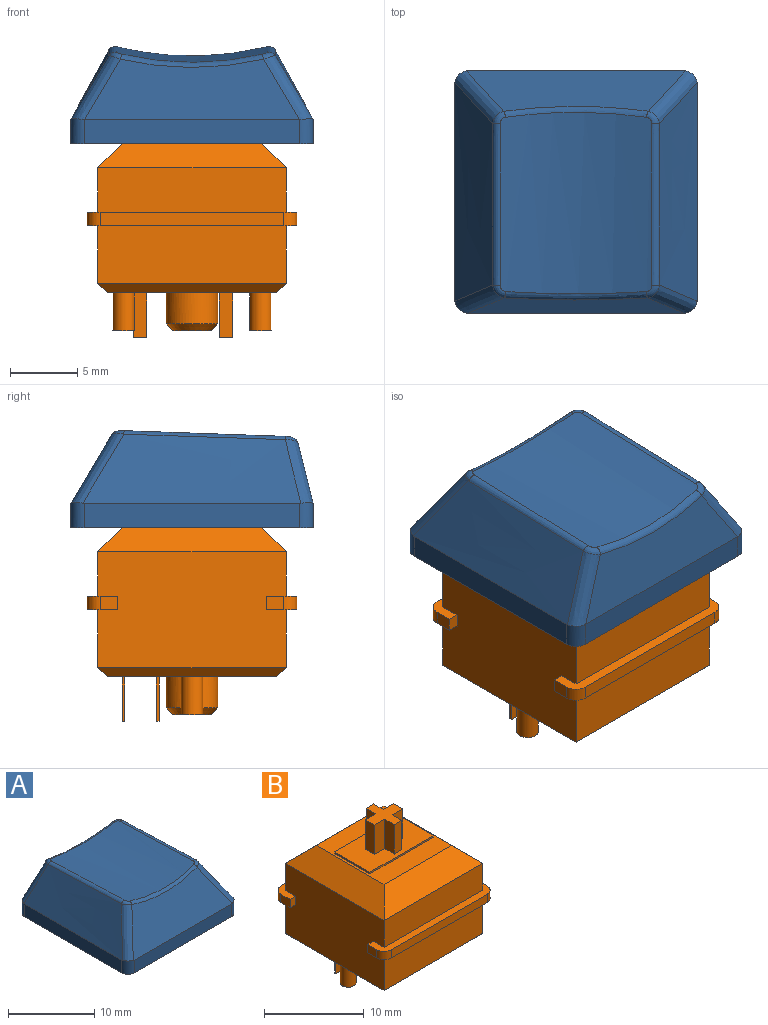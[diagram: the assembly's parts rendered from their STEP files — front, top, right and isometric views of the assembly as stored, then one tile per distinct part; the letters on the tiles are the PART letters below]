
ASSEMBLY  parts=2 mates=1
PART A: 50 faces, bbox 21.6x21x10.3 mm
  f0: plane 18x18mm, normal (0,0,-1), area 67.1mm2, adj f1,f2,f3,f4,f10,f12,f14,f16
  f1: plane 16x1.8mm, normal (1,0,0), area 28.8mm2, adj f0,f8,f10,f16
  f2: plane 16x1.8mm, normal (0,1,0), area 28.8mm2, adj f0,f5,f14,f15,f16,f17
  f3: plane 16x1.8mm, normal (-1,0,0), area 28.8mm2, adj f0,f6,f12,f14
  f4: plane 16x1.8mm, normal (0,-1,0), area 28.8mm2, adj f0,f7,f10,f12
  f5: plane 15.96x4.48mm, normal (0,0.97,0.24), area 56.8mm2, adj f2,f15,f17,f20
  f6: bspline ~18x5.51mm, area 80.2mm2, adj f3,f12,f13,f14,f15,f19
  f7: plane 16.27x5.09mm, normal (0,-0.86,0.51), area 74.6mm2, adj f4,f10,f11,f12,f13,f23
  f8: bspline ~18x5.51mm, area 80.2mm2, adj f1,f10,f11,f16,f17,f24
  f9: cylinder r=22.9mm len=13.32mm, axis (0,1,-0.04), area 149.5mm2, adj f18,f19,f20,f21,f22,f23,f24,f25
  f10: cylinder r=1mm len=1.89mm, axis (0,0,-1), area 2.9mm2, adj f0,f1,f4,f7,f8,f11
  f11: bspline ~6.77x4.7mm, area 8.7mm2, adj f7,f8,f10,f25
  f12: cylinder r=1mm len=1.89mm, axis (0,0,1), area 2.9mm2, adj f0,f3,f4,f6,f7,f13
  f13: bspline ~6.77x4.7mm, area 8.7mm2, adj f6,f7,f12,f21
  f14: cylinder r=1mm len=1.81mm, axis (0,0,-1), area 2.8mm2, adj f0,f2,f3,f6,f15
  f15: bspline ~8.13x5.44mm, area 7.9mm2, adj f2,f5,f6,f14,f18
  f16: cylinder r=1mm len=1.81mm, axis (0,0,1), area 2.8mm2, adj f0,f1,f2,f8,f17
  f17: bspline ~8.13x5.44mm, area 7.9mm2, adj f2,f5,f8,f16,f22
  f18: bspline ~1.19x1.01mm, area 0.7mm2, adj f9,f15,f19,f20
  f19: bspline ~16.72x0.91mm, area 7.8mm2, adj f6,f9,f18,f21
  f20: bspline ~10.66x0.99mm, area 6.9mm2, adj f5,f9,f18,f22
  f21: bspline ~1.2x1.09mm, area 0.6mm2, adj f9,f13,f19,f23
  f22: bspline ~1.17x1.02mm, area 0.7mm2, adj f9,f17,f20,f24
  f23: bspline ~10.72x0.84mm, area 5.8mm2, adj f7,f9,f21,f25
  f24: bspline ~16.72x0.91mm, area 7.8mm2, adj f8,f9,f22,f25
  f25: bspline ~1.2x1.09mm, area 0.6mm2, adj f9,f11,f23,f24
  f26: plane 16.02x1.56mm, normal (-1,0,0), area 24.6mm2, adj f0,f27,f29,f33
  f27: plane 16x1.68mm, normal (0,-1,0), area 26.8mm2, adj f0,f26,f28,f30,f31,f33
  f28: plane 16.02x1.56mm, normal (1,0,0), area 24.6mm2, adj f0,f27,f29,f31
  f29: plane 16.02x1.54mm, normal (0,1,0), area 24.4mm2, adj f0,f26,f28,f32
  f30: plane 16.19x4.4mm, normal (0,-0.97,-0.24), area 50.7mm2, adj f27,f31,f33,f34
  f31: offset ~20x7.51mm, area 71.4mm2, adj f27,f28,f30,f32,f34
  f32: plane 16.71x5.3mm, normal (0,0.86,-0.51), area 66.9mm2, adj f29,f31,f33,f34
  f33: offset ~20x7.51mm, area 71.4mm2, adj f26,f27,f30,f32,f34
  f34: cylinder r=23.9mm len=12.29mm, axis (0,1,-0.04), area 112.6mm2, adj f30,f31,f32,f33,f46
  f35: plane 4.69x1.5mm, normal (-1,0,0), area 7mm2, adj f36,f44,f45,f49
  f36: plane 4.78x1.5mm, normal (0,-1,0), area 7.1mm2, adj f35,f37,f45,f49
  f37: plane 4.82x1.3mm, normal (-1,0,0), area 6.2mm2, adj f36,f38,f45,f49
  f38: plane 4.82x1.5mm, normal (0,1,0), area 7.2mm2, adj f37,f39,f45,f49
  f39: plane 4.79x1.5mm, normal (-1,0,0), area 7.1mm2, adj f38,f40,f45,f49
  f40: plane 4.79x1.3mm, normal (0,1,0), area 6.2mm2, adj f39,f41,f45,f49
  f41: plane 4.79x1.5mm, normal (1,0,0), area 7.1mm2, adj f40,f42,f45,f49
  f42: plane 4.82x1.5mm, normal (0,1,0), area 7.2mm2, adj f41,f43,f45,f49
  f43: plane 4.82x1.3mm, normal (1,0,0), area 6.2mm2, adj f42,f45,f47,f49
  f44: plane 4.64x1.3mm, normal (0,-1,0), area 6mm2, adj f35,f45,f48,f49
  f45: plane 5.5x5.5mm, normal (0,0,-1), area 14.3mm2, adj f35,f36,f37,f38,f39,f40,f41,f42
  f46: cylinder r=2.75mm len=5.5mm, axis (0,0,-1), area 84mm2, adj f34,f45
  f47: plane 4.78x1.5mm, normal (0,-1,0), area 7.1mm2, adj f43,f45,f48,f49
  f48: plane 4.69x1.5mm, normal (1,0,0), area 7mm2, adj f44,f45,f47,f49
  f49: cylinder r=23.9mm len=4.3mm, axis (0,1,-0.04), area 9.5mm2, adj f35,f36,f37,f38,f39,f40,f41,f42
PART B: 69 faces, bbox 15.6x15.6x18.6 mm
  f0: plane 15.6x2.3mm, normal (0,0,-1), area 14.4mm2, adj f2,f3,f28,f30,f35,f60,f62,f63
  f1: plane 15.6x2.3mm, normal (0,0,-1), area 14.4mm2, adj f28,f30,f33,f34,f36,f59,f61,f64
  f2: plane 1.3x1mm, normal (1,0,0), area 1.3mm2, adj f0,f32,f62,f66
  f3: plane 1.3x1mm, normal (-1,0,0), area 1.3mm2, adj f0,f32,f63,f68
  f4: plane 15.6x2.3mm, normal (0,0,1), area 14.4mm2, adj f28,f30,f31,f33,f34,f36,f61,f64
  f5: plane 14x2.2mm, normal (-0.71,0,0.71), area 36.7mm2, adj f6,f7,f26,f30
  f6: plane 14x2.2mm, normal (0,-0.71,0.71), area 36.7mm2, adj f5,f7,f27,f31
  f7: plane 9.6x9.6mm, normal (0,0,1), area 47.2mm2, adj f5,f6,f8,f9,f10,f11,f26,f27
  f8: plane 5x0.2mm, normal (1,0,0), area 1mm2, adj f7,f9,f11,f12
  f9: plane 9x0.2mm, normal (0,1,0), area 1.8mm2, adj f7,f8,f10,f12
  f10: plane 5x0.2mm, normal (-1,0,0), area 1mm2, adj f7,f9,f11,f12
  f11: plane 9x0.2mm, normal (0,-1,0), area 1.8mm2, adj f7,f8,f10,f12
  f12: plane 9x5mm, normal (0,0,1), area 36.9mm2, adj f8,f9,f10,f11,f13,f14,f15,f16
  f13: plane 3.6x1.35mm, normal (1,0,0), area 4.9mm2, adj f12,f14,f24,f25
  f14: plane 3.6x1.08mm, normal (0,1,0), area 3.9mm2, adj f12,f13,f15,f25
  f15: plane 3.6x1.35mm, normal (-1,0,0), area 4.9mm2, adj f12,f14,f16,f25
  f16: plane 3.6x1.46mm, normal (0,1,0), area 5.3mm2, adj f12,f15,f17,f25
  f17: plane 3.6x1.3mm, normal (-1,0,0), area 4.7mm2, adj f12,f16,f18,f25
  f18: plane 3.6x1.46mm, normal (0,-1,0), area 5.3mm2, adj f12,f17,f19,f25
  f19: plane 3.6x1.35mm, normal (-1,0,0), area 4.9mm2, adj f12,f18,f20,f25
  f20: plane 3.6x1.08mm, normal (0,-1,0), area 3.9mm2, adj f12,f19,f21,f25
  f21: plane 3.6x1.35mm, normal (1,0,0), area 4.9mm2, adj f12,f20,f22,f25
  f22: plane 3.6x1.46mm, normal (0,-1,0), area 5.3mm2, adj f12,f21,f23,f25
  f23: plane 3.6x1.3mm, normal (1,0,0), area 4.7mm2, adj f12,f22,f24,f25
  f24: plane 3.6x1.46mm, normal (0,1,0), area 5.3mm2, adj f12,f13,f23,f25
  f25: plane 4x4mm, normal (0,0,1), area 8.1mm2, adj f13,f14,f15,f16,f17,f18,f19,f20
  f26: plane 14x2.2mm, normal (0,0.71,0.71), area 36.7mm2, adj f5,f7,f27,f29
  f27: plane 14x2.2mm, normal (0.71,0,0.71), area 36.7mm2, adj f6,f7,f26,f28
  f28: plane 14x8.6mm, normal (1,0,0), area 117.4mm2, adj f0,f1,f4,f27,f29,f31,f32,f55
  f29: plane 14x3.3mm, normal (0,1,0), area 46.2mm2, adj f26,f28,f30,f32
  f30: plane 14x8.6mm, normal (-1,0,0), area 117.4mm2, adj f0,f1,f4,f5,f29,f31,f32,f57
  f31: plane 14x3.3mm, normal (0,-1,0), area 46.2mm2, adj f4,f6,f28,f30
  f32: plane 15.6x2.3mm, normal (0,0,1), area 14.4mm2, adj f2,f3,f28,f29,f30,f35,f62,f63
  f33: plane 13.6x1mm, normal (0,-1,0), area 13.6mm2, adj f1,f4,f61,f64
  f34: plane 1.3x1mm, normal (1,0,0), area 1.3mm2, adj f1,f4,f61,f65
  f35: plane 13.6x1mm, normal (0,1,0), area 13.6mm2, adj f0,f32,f62,f63
  f36: plane 1.3x1mm, normal (-1,0,0), area 1.3mm2, adj f1,f4,f64,f67
  f37: plane 2.85x2.85mm, normal (0,0,-1), area 6.4mm2, adj f38
  f38: cone r=1.43mm half-angle=45deg, axis (0,0,1), area 7.4mm2, adj f37,f43
  f39: plane 1x0.2mm, normal (0,0,-1), area 0.2mm2, adj f44,f45,f46,f47
  f40: plane 1x0.2mm, normal (0,0,-1), area 0.2mm2, adj f48,f49,f50,f51
  f41: plane 1.6x1.6mm, normal (0,0,-1), area 2mm2, adj f52
  f42: plane 1.6x1.6mm, normal (0,0,-1), area 2mm2, adj f53
  f43: cylinder r=1.93mm len=3.85mm, axis (0,0,1), area 27.8mm2, adj f38,f54
  f44: plane 3.3x0.2mm, normal (-1,0,0), area 0.7mm2, adj f39,f45,f47,f54
  f45: plane 3.3x1mm, normal (0,1,0), area 3.3mm2, adj f39,f44,f46,f54
  f46: plane 3.3x0.2mm, normal (1,0,0), area 0.7mm2, adj f39,f45,f47,f54
  f47: plane 3.3x1mm, normal (0,-1,0), area 3.3mm2, adj f39,f44,f46,f54
  f48: plane 3.3x0.2mm, normal (-1,0,0), area 0.7mm2, adj f40,f49,f51,f54
  f49: plane 3.3x1mm, normal (0,1,0), area 3.3mm2, adj f40,f48,f50,f54
  f50: plane 3.3x0.2mm, normal (1,0,0), area 0.7mm2, adj f40,f49,f51,f54
  f51: plane 3.3x1mm, normal (0,-1,0), area 3.3mm2, adj f40,f48,f50,f54
  f52: cylinder r=0.8mm len=2.8mm, axis (0,0,1), area 14.1mm2, adj f41,f54
  f53: cylinder r=0.8mm len=2.8mm, axis (0,0,1), area 14.1mm2, adj f42,f54
  f54: plane 12.6x12.6mm, normal (0,0,-1), area 142.7mm2, adj f43,f44,f45,f46,f47,f48,f49,f50
  f55: plane 14x0.7mm, normal (0.71,0,-0.71), area 13.2mm2, adj f28,f54,f56,f58
  f56: plane 14x0.7mm, normal (0,0.71,-0.71), area 13.2mm2, adj f54,f55,f57,f60
  f57: plane 14x0.7mm, normal (-0.71,0,-0.71), area 13.2mm2, adj f30,f54,f56,f58
  f58: plane 14x0.7mm, normal (0,-0.71,-0.71), area 13.2mm2, adj f54,f55,f57,f59
  f59: plane 14x4.3mm, normal (0,-1,0), area 60.2mm2, adj f1,f28,f30,f58
  f60: plane 14x4.3mm, normal (0,1,0), area 60.2mm2, adj f0,f28,f30,f56
  f61: cylinder r=1mm len=1mm, axis (0,0,-1), area 1.6mm2, adj f1,f4,f33,f34
  f62: cylinder r=1mm len=1mm, axis (0,0,1), area 1.6mm2, adj f0,f2,f32,f35
  f63: cylinder r=1mm len=1mm, axis (0,0,-1), area 1.6mm2, adj f0,f3,f32,f35
  f64: cylinder r=1mm len=1mm, axis (0,0,1), area 1.6mm2, adj f1,f4,f33,f36
  f65: plane 1x0.8mm, normal (0,1,0), area 0.8mm2, adj f1,f4,f28,f34
  f66: plane 1x0.8mm, normal (0,-1,0), area 0.8mm2, adj f0,f2,f28,f32
  f67: plane 1x0.8mm, normal (0,1,0), area 0.8mm2, adj f1,f4,f30,f36
  f68: plane 1x0.8mm, normal (0,-1,0), area 0.8mm2, adj f0,f3,f30,f32
PLACE A rot(axis=(0,0,1),180deg) t=(0,0,11.1)mm
PLACE B at identity fixed
MATE fastened B.f38 <-> A.f46  axis (0,0,1) through (0,0,11.7)mm
